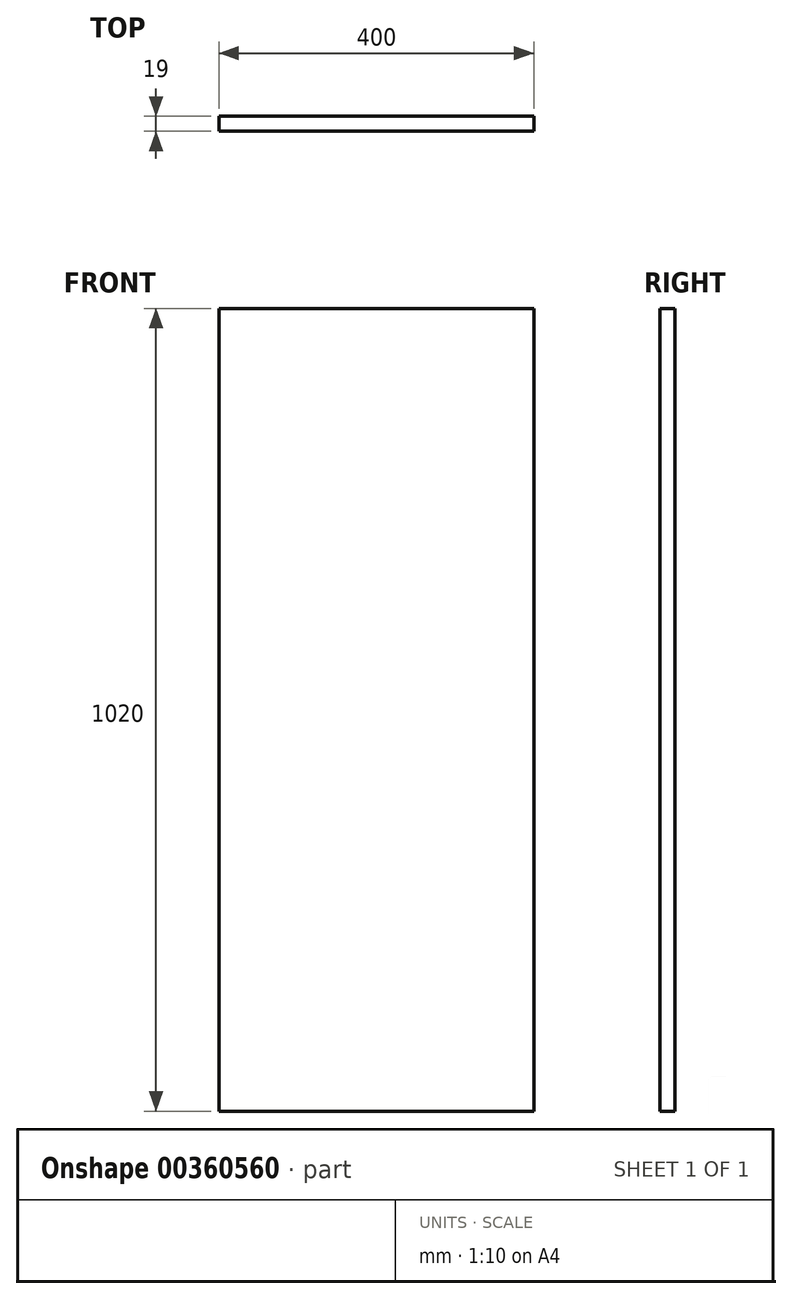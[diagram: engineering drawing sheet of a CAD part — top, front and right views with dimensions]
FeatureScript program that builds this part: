
annotation { "Feature Type Name" : "Feature", "Feature Type Description" : "" }
export const myFeature = defineFeature(function(context is Context, id is Id, definition is map)
    precondition{}
    {
        {
            var Q0;
            Q0=qCreatedBy(makeId("Front.planeOp"),FACE);
            var sketch = newSketch(context, id + "F0", { "sketchPlane" : qUnion([Q0])});
            skLineSegment(sketch, "E0.bottom", {"start": v(0, 0) * mm, "end": v(400, 0) * mm});
            skLineSegment(sketch, "E0.top", {"start": v(0, 1020) * mm, "end": v(400, 1020) * mm});
            skLineSegment(sketch, "E0.left", {"start": v(0, 0) * mm, "end": v(0, 1020) * mm});
            skLineSegment(sketch, "E0.right", {"start": v(400, 0) * mm, "end": v(400, 1020) * mm});
            skSolve(sketch);
        }
        {
            var Q0;
            Q0=makeQuery(id+"F0.imprint","IMPRINT",FACE,{"disambiguationData":[TD([[makeQuery(id+"F0.imprint","IMPRINT",EDGE,{"derivedFrom":sQuery(id+"F0.wireOp",EDGE,"E0.bottom")}),1.0]])]});
            extrude(context, id + "F1", {"entities" : qUnion([Q0]), "depth" : 19 * mm});
        }
    });
